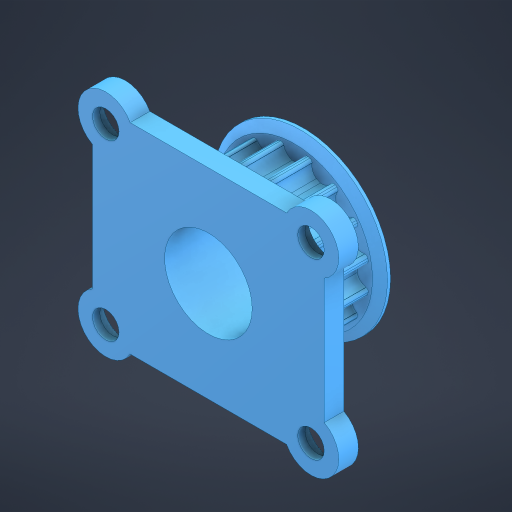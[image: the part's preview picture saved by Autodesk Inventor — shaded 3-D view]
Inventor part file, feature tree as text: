
AUTODESK INVENTOR PART (.ipt)
format: ipt  version: 2024.2 (Build 282272000, 272)  size: 509,952 bytes
history: native  units: in
note: dims shown in document units (in); Inventor stores cm internally (conversion verified against a paired STEP export)
features: extrude x4, sketch x3, other x2
ambient origin geometry x8: Origin, YZ Plane, XZ Plane, XY Plane, X Axis, Y Axis, Z Axis, Center Point
bodies: Solid1 (feature_tree)
feature tree (9):
  other  "HTD Pulley - 5mm.step"
  extrude  "Extrusion1"  Depth=0.1693in
  sketch  "Sketch2"  dims[d2=0.1693in d3=0.1693in]
  extrude  "Extrusion4"  Depth=0.1693in
  extrude  "Extrusion2"  TaperAngle=0.0deg  [1 undecoded]
  extrude  "Extrusion3"  TaperAngle=0.0deg  [1 undecoded]
  sketch  "Sketch1"  dims[d0=0.1693in d1=0.1693in]
  sketch  "Sketch3"  dims[d4=0.0in d5=0.0in d6=0.0in d7=0.0in d9=0.5545in d10=0.5545in d11=0.6545in d12=0.6545in d15=0.125in d16=0.0in d18=0.2953in d19=0.2953in d20=0.2953in d21=0.2953in d22=0.0787in d23=0.0in d24=0.5591in d25=0.0in d26=0.0in d33=0.3543in d34=0.3543in d35=0.3543in d36=0.3543in d37=0.0in d38=0.0in d39=0.0in d40=0.0in d41=0.0in]
  other  "Part 1"
note: 2 required parameter values undecoded (feature->parameter linkage not recoverable at this tier; creation-order binding heuristic only, values carry confidence <= 0.55)
